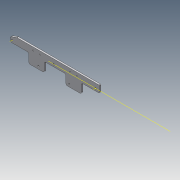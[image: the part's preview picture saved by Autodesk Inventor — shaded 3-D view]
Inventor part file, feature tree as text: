
AUTODESK INVENTOR PART (.ipt)
format: ipt  version: 2020.3 (Build 243373000, 373)  size: 193,024 bytes
history: native  units: in
note: dims shown in document units (in); Inventor stores cm internally (conversion verified against a paired STEP export)
features: extrude x3, other x3, hole x2, fillet x2, chamfer x1, pattern_linear x1
ambient origin geometry x8: Origin, YZ Plane, XZ Plane, XY Plane, X Axis, Y Axis, Z Axis, Center Point
bodies: Solid1 (feature_tree)
feature tree (12):
  extrude  "Extrusion1"  Depth=6.75in
  extrude  "Extrusion2"  Depth=2.5in
  hole  "Hole3"  [1 undecoded]
  chamfer  "Chamfer1"  Distance=0.125in
  fillet  "Fillet1"  Radius=0.125in
  fillet  "Fillet2"  Radius=0.75in
  pattern_linear  "Rectangular Pattern1"  Spacing1=0.375in  [1 undecoded]
  hole  "Hole1"  [1 undecoded]
  extrude  "Extrusion3"  Depth=7.375in
  other  "Work Axis1"
  other  "Work Axis3"
  other  "Work Axis4"
note: 3 required parameter values undecoded (feature->parameter linkage not recoverable at this tier; creation-order binding heuristic only, values carry confidence <= 0.55)
